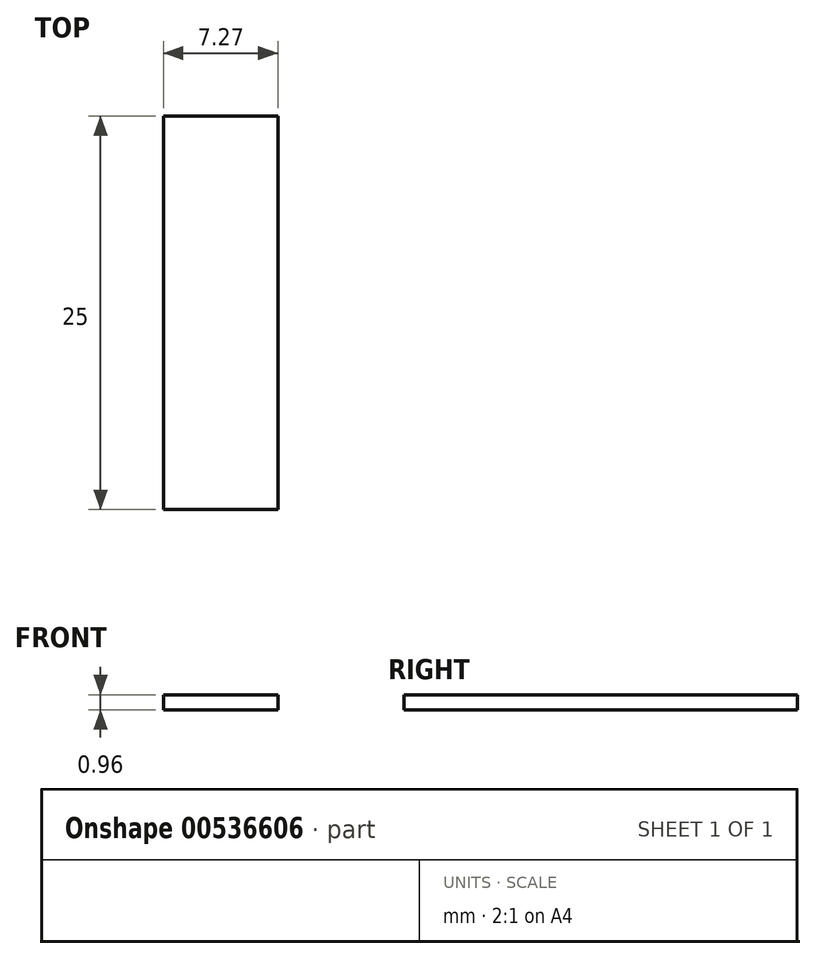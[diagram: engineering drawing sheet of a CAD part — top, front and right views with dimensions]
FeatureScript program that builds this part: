
annotation { "Feature Type Name" : "Feature", "Feature Type Description" : "" }
export const myFeature = defineFeature(function(context is Context, id is Id, definition is map)
    precondition{}
    {
        {
            var Q0;
            Q0=qCreatedBy(makeId("Front.planeOp"),FACE);
            var sketch = newSketch(context, id + "F0", { "sketchPlane" : qUnion([Q0])});
            skLineSegment(sketch, "E0.bottom", {"start": v(0, 0) * mm, "end": v(7.27, 0) * mm});
            skLineSegment(sketch, "E0.top", {"start": v(0, 0.96) * mm, "end": v(7.27, 0.96) * mm});
            skLineSegment(sketch, "E0.left", {"start": v(0, 0) * mm, "end": v(0, 0.96) * mm});
            skLineSegment(sketch, "E0.right", {"start": v(7.27, 0) * mm, "end": v(7.27, 0.96) * mm});
            skLineSegment(sketch, "E1.bottom", {"start": v(7.27, 8.07) * mm, "end": v(6.12, 8.07) * mm});
            skLineSegment(sketch, "E1.top", {"start": v(7.27, 0.96) * mm, "end": v(6.12, 0.96) * mm});
            skLineSegment(sketch, "E1.left", {"start": v(7.27, 8.07) * mm, "end": v(7.27, 0.96) * mm});
            skLineSegment(sketch, "E1.right", {"start": v(6.12, 8.07) * mm, "end": v(6.12, 0.96) * mm});
            skLineSegment(sketch, "E2.bottom", {"start": v(6.12, 2.35) * mm, "end": v(5.08, 2.35) * mm});
            skLineSegment(sketch, "E2.top", {"start": v(6.12, 5.2) * mm, "end": v(5.08, 5.2) * mm});
            skLineSegment(sketch, "E2.left", {"start": v(6.12, 2.35) * mm, "end": v(6.12, 5.2) * mm});
            skLineSegment(sketch, "E2.right", {"start": v(5.08, 2.35) * mm, "end": v(5.08, 5.2) * mm});
            skSolve(sketch);
        }
        {
            var Q0;
            Q0=makeQuery(id+"F0.imprint","IMPRINT",FACE,{"disambiguationData":[TD([[makeQuery(id+"F0.imprint","IMPRINT",EDGE,{"derivedFrom":sQuery(id+"F0.wireOp",EDGE,"E0.bottom")}),1.0]])]});
            extrude(context, id + "F1", {"entities" : qUnion([Q0]), "depth" : 25 * mm, "offsetDistance" : 25 * mm});
        }
    });
